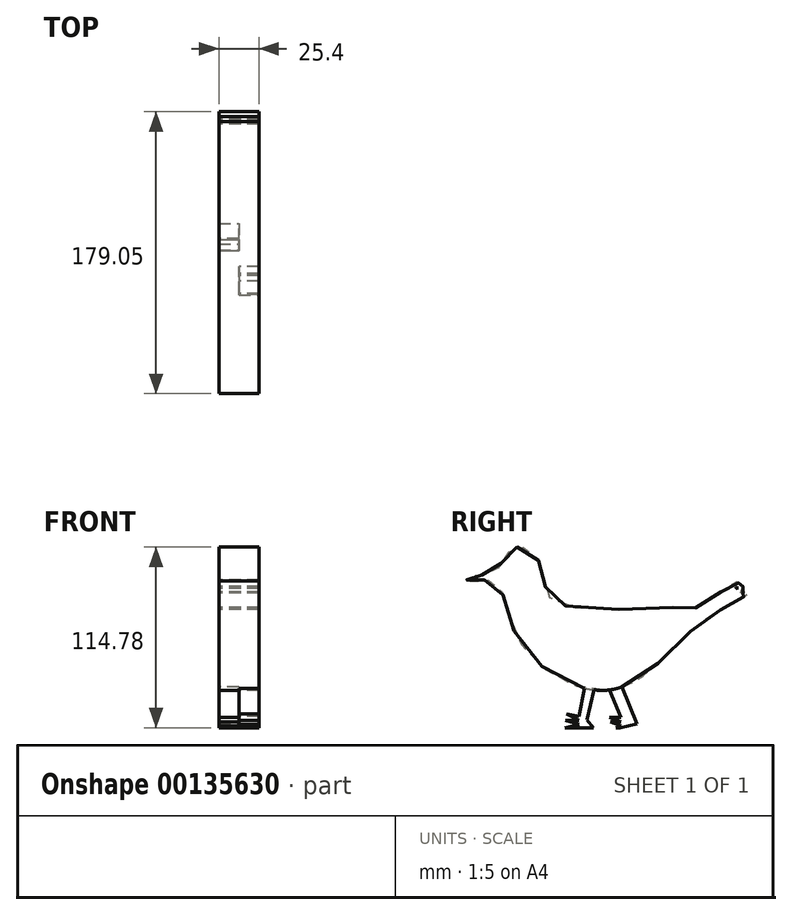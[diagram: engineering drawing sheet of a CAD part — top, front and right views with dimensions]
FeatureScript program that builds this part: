
annotation { "Feature Type Name" : "Feature", "Feature Type Description" : "" }
export const myFeature = defineFeature(function(context is Context, id is Id, definition is map)
    precondition{}
    {
        {
            var Q0;
            Q0=qCreatedBy(makeId("Right.planeOp"),FACE);
            var sketch = newSketch(context, id + "F0", { "sketchPlane" : qUnion([Q0])});
            skFitSpline(sketch, "E0", {"points": [v(41.12, 19.51) * mm, v(-42.17, 23.18) * mm, v(-50.02, 45.44) * mm, v(-67.3, 57.49) * mm, v(-80.4, 42.3) * mm, v(-95.6, 39.15) * mm, v(-97.69, 36.53) * mm, v(-80.93, 35.75) * mm, v(-65.47, 0) * mm, v(-5.24, -32.6) * mm, v(48.98, 8.25) * mm, v(77.26, 25.54) * mm, v(80.93, 29.46) * mm, v(76.21, 28.94) * mm, v(78.05, 32.87) * mm, v(73.33, 31.82) * mm, v(74.9, 36.01) * mm, v(50.02, 20.3) * mm, v(41.12, 19.51) * mm]});
            skLineSegment(sketch, "E1", {"start": v(-5.24, -32.6) * mm, "end": v(-5.24, -44.65) * mm});
            skLineSegment(sketch, "E2", {"start": v(-5.24, -44.65) * mm, "end": v(-17.8, -42.56) * mm});
            skLineSegment(sketch, "E3", {"start": v(-17.8, -42.56) * mm, "end": v(-6.02, -47.27) * mm});
            skLineSegment(sketch, "E4", {"start": v(-6.02, -47.27) * mm, "end": v(-18.07, -47.27) * mm});
            skLineSegment(sketch, "E5", {"start": v(-18.07, -47.27) * mm, "end": v(-6.55, -49.9) * mm});
            skLineSegment(sketch, "E6", {"start": v(-6.55, -49.9) * mm, "end": v(-16.24, -49.9) * mm});
            skLineSegment(sketch, "E7", {"start": v(-16.24, -49.9) * mm, "end": v(0, -52.25) * mm});
            skLineSegment(sketch, "E8", {"start": v(0, -52.25) * mm, "end": v(-2.36, -45.7) * mm});
            skLineSegment(sketch, "E9", {"start": v(-2.36, -45.7) * mm, "end": v(0, -31.3) * mm});
            skSolve(sketch);
        }
        {
            var Q0;
            {var subQ0=sQuery(id+"F0.wireOp",EDGE,"E0");var subQ1=makeQuery(id+"F0.imprint","INTERSECT",VERTEX,{"derivedFrom":[subQ0,sQuery(id+"F0.wireOp",EDGE,"E1")]});Q0=makeQuery(id+"F0.imprint","IMPRINT",FACE,{"disambiguationData":[TD([[makeQuery(id+"F0.imprint","IMPRINT",EDGE,{"disambiguationData":[TD([[subQ1,-1.0]])],"derivedFrom":subQ0}),1.0]])]});}
            extrude(context, id + "F1", {"entities" : qUnion([Q0]), "endBound" : BoundingType.SYMMETRIC, "depth" : 25.4 * mm});
        }
        {
            var Q0;
            Q0=qCreatedBy(makeId("Right.planeOp"),FACE);
            var sketch = newSketch(context, id + "F2", { "sketchPlane" : qUnion([Q0])});
            skLineSegment(sketch, "E10", {"start": v(-22.76, -30.51) * mm, "end": v(-26.43, -49.63) * mm});
            skLineSegment(sketch, "E11", {"start": v(-26.43, -49.63) * mm, "end": v(-34.3, -48.12) * mm});
            skLineSegment(sketch, "E12", {"start": v(-34.3, -48.12) * mm, "end": v(-26.43, -52.25) * mm});
            skLineSegment(sketch, "E13", {"start": v(-26.43, -52.25) * mm, "end": v(-35.07, -52.25) * mm});
            skLineSegment(sketch, "E14", {"start": v(-35.07, -52.25) * mm, "end": v(-26.43, -54.87) * mm});
            skLineSegment(sketch, "E15", {"start": v(-26.43, -54.87) * mm, "end": v(-35.33, -56.96) * mm});
            skLineSegment(sketch, "E16", {"start": v(-35.33, -56.96) * mm, "end": v(-17.26, -56.96) * mm});
            skLineSegment(sketch, "E17", {"start": v(-17.26, -56.96) * mm, "end": v(-21.45, -51.99) * mm});
            skLineSegment(sketch, "E18", {"start": v(-21.45, -51.99) * mm, "end": v(-16.74, -31.56) * mm});
            skLineSegment(sketch, "E19", {"start": v(-16.74, -31.56) * mm, "end": v(-22.76, -30.51) * mm});
            skSolve(sketch);
        }
        {
            var Q0;
            Q0 = qSketchRegion(id + "F2", true);
            extrude(context, id + "F3", {"entities" : qUnion([Q0]), "operationType" : NewBodyOperationType.ADD, "depth" : 12.7 * mm});
        }
        {
            var Q0;
            Q0=qCreatedBy(makeId("Right.planeOp"),FACE);
            var sketch = newSketch(context, id + "F4", { "sketchPlane" : qUnion([Q0])});
            skLineSegment(sketch, "E20", {"start": v(-7.57, -32.08) * mm, "end": v(0, -50.42) * mm});
            skLineSegment(sketch, "E21", {"start": v(0, -50.42) * mm, "end": v(-7.05, -50.42) * mm});
            skLineSegment(sketch, "E22", {"start": v(-7.05, -50.42) * mm, "end": v(0, -53.3) * mm});
            skLineSegment(sketch, "E23", {"start": v(0, -53.3) * mm, "end": v(-6.52, -53.3) * mm});
            skLineSegment(sketch, "E24", {"start": v(-6.52, -53.3) * mm, "end": v(0, -55.65) * mm});
            skLineSegment(sketch, "E25", {"start": v(0, -55.65) * mm, "end": v(-5.74, -58.27) * mm});
            skLineSegment(sketch, "E26", {"start": v(-5.74, -58.27) * mm, "end": v(10.24, -54.34) * mm});
            skLineSegment(sketch, "E27", {"start": v(10.24, -54.34) * mm, "end": v(0, -29.2) * mm});
            skLineSegment(sketch, "E28", {"start": v(0, -29.2) * mm, "end": v(-7.57, -32.08) * mm});
            skSolve(sketch);
        }
        {
            var Q0;
            Q0=makeQuery(id+"F4.imprint","IMPRINT",FACE,{"disambiguationData":[TD([[makeQuery(id+"F4.imprint","IMPRINT",EDGE,{"derivedFrom":sQuery(id+"F4.wireOp",EDGE,"E20")}),1.0]])]});
            extrude(context, id + "F5", {"entities" : qUnion([Q0]), "operationType" : NewBodyOperationType.ADD, "oppositeDirection" : true, "depth" : 12.7 * mm});
        }
        {
            var Q0;
            Q0=qCreatedBy(makeId("Front.planeOp"),FACE);
            var sketch = newSketch(context, id + "F6", { "sketchPlane" : qUnion([Q0])});
            skLineSegment(sketch, "E29", {"start": v(14.78, -56.95) * mm, "end": v(-17.88, -56.95) * mm});
            skLineSegment(sketch, "E30.bottom", {"start": v(14.78, -56.95) * mm, "end": v(-22.5, -56.95) * mm});
            skLineSegment(sketch, "E30.top", {"start": v(14.78, -67.18) * mm, "end": v(-22.5, -67.18) * mm});
            skLineSegment(sketch, "E30.left", {"start": v(14.78, -56.95) * mm, "end": v(14.78, -67.18) * mm});
            skLineSegment(sketch, "E30.right", {"start": v(-22.5, -56.95) * mm, "end": v(-22.5, -67.18) * mm});
            skSolve(sketch);
        }
        {
            var Q0;
            Q0 = qSketchRegion(id + "F6", true);
            extrude(context, id + "F7", {"entities" : qUnion([Q0]), "operationType" : NewBodyOperationType.REMOVE, "endBound" : BoundingType.SYMMETRIC, "depth" : 103.27 * mm});
        }
    });
